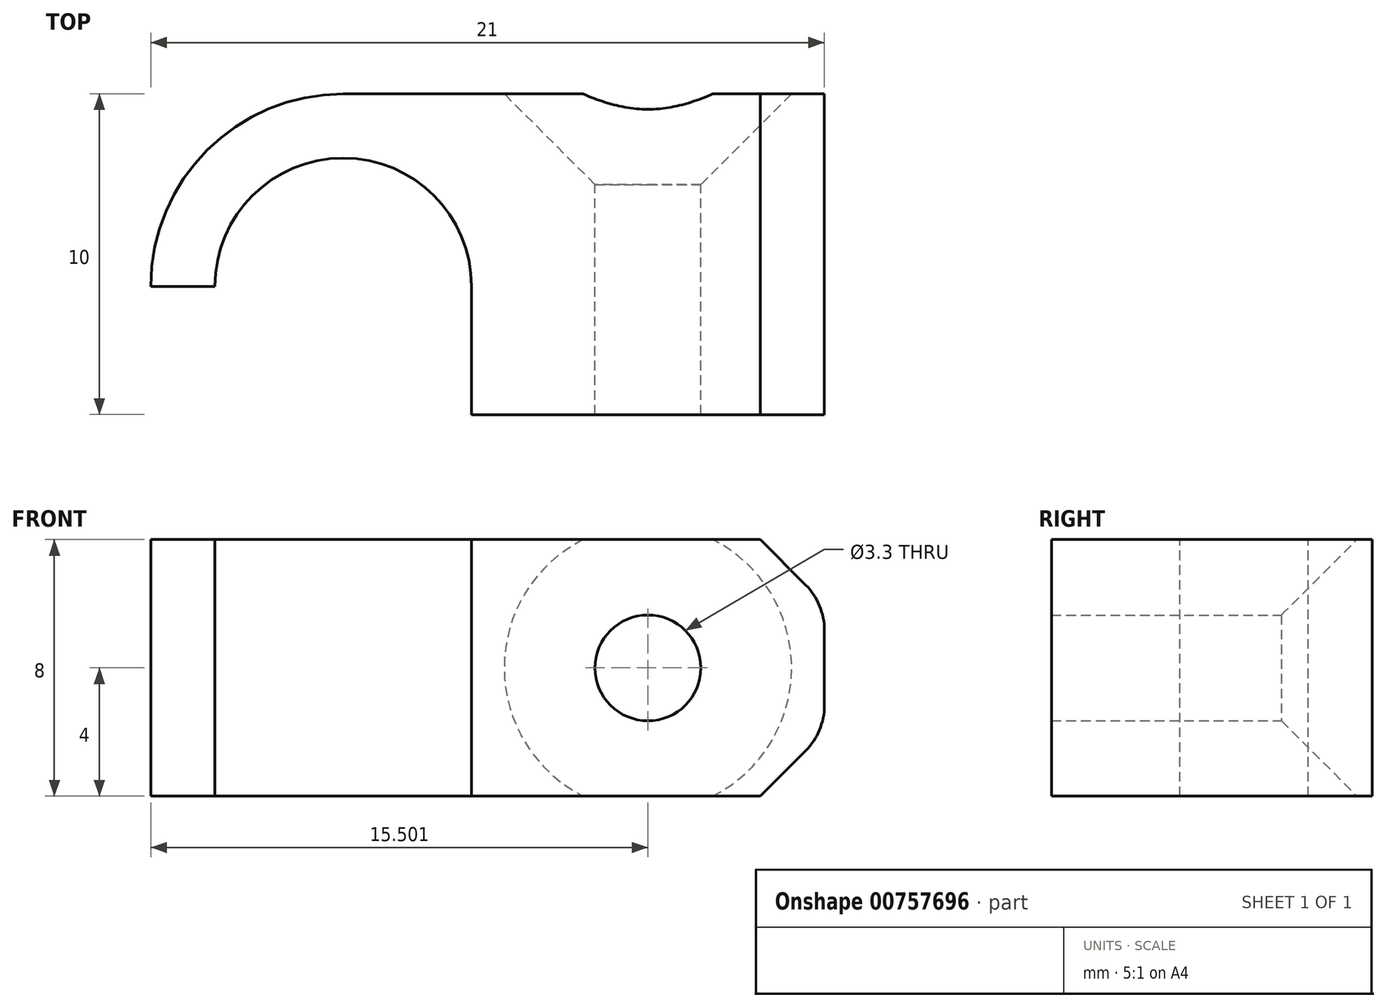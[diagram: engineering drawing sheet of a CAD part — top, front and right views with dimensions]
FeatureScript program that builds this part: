
annotation { "Feature Type Name" : "Feature", "Feature Type Description" : "" }
export const myFeature = defineFeature(function(context is Context, id is Id, definition is map)
    precondition{}
    {
        {
            var Q0;
            Q0=qCreatedBy(makeId("Top.planeOp"),FACE);
            var sketch = newSketch(context, id + "F0", { "sketchPlane" : qUnion([Q0])});
            skArc(sketch, "E0", {"start": v(-7.6, 12.22) * mm, "mid": v(-11.6, 16.22) * mm, "end": v(-15.6, 12.22) * mm});
            skArc(sketch, "E1.0", {"start": v(-11.6, 18.22) * mm, "mid": v(-15.84, 16.46) * mm, "end": v(-17.6, 12.22) * mm});
            skLineSegment(sketch, "E2", {"start": v(-11.6, 18.22) * mm, "end": v(3.4, 18.22) * mm});
            skLineSegment(sketch, "E3", {"start": v(3.4, 18.22) * mm, "end": v(3.4, 8.22) * mm});
            skLineSegment(sketch, "E4", {"start": v(3.4, 8.22) * mm, "end": v(-7.6, 8.22) * mm});
            skLineSegment(sketch, "E5", {"start": v(-17.6, 12.22) * mm, "end": v(-15.6, 12.22) * mm});
            skLineSegment(sketch, "E6", {"start": v(-7.6, 12.22) * mm, "end": v(-7.6, 8.22) * mm});
            skPoint(sketch, "E7.orphan", {"position": v(-11.6, 8.22) * mm});
            skSolve(sketch);
        }
        {
            var Q0;
            Q0 = qSketchRegion(id + "F0", true);
            extrude(context, id + "F1", {"entities" : qUnion([Q0]), "endBound" : BoundingType.SYMMETRIC, "oppositeDirection" : true, "depth" : 8 * mm, "offsetDistance" : 25 * mm});
        }
        {
            var Q0;
            Q0=makeQuery(id+"F1.opExtrude","SWEPT_FACE",FACE,{"disambiguationData":[OSD([sQuery(id+"F0.wireOp",EDGE,"E2")])]});
            var sketch = newSketch(context, id + "F2", { "sketchPlane" : qUnion([Q0])});
            skLineSegment(sketch, "E8", {"start": v(-3.4, 4) * mm, "end": v(7.6, -4) * mm, "construction": true});
            skPoint(sketch, "E9", {"position": v(2.1, 0) * mm});
            skSolve(sketch);
        }
        {
            var Q0;
            Q0=sQuery(id+"F2.wireOp",VERTEX,"E9");
            var Q1;
            Q1=makeQuery(id+"F1.opExtrude","SWEPT_BODY",BODY,{"disambiguationData":[OSD([sQuery(id+"F0.wireOp",EDGE,"E0"),sQuery(id+"F0.wireOp",EDGE,"E1.0"),sQuery(id+"F0.wireOp",EDGE,"E2"),sQuery(id+"F0.wireOp",EDGE,"E3"),sQuery(id+"F0.wireOp",EDGE,"E4"),sQuery(id+"F0.wireOp",EDGE,"E5"),sQuery(id+"F0.wireOp",EDGE,"E6")])]});
            hole(context, id + "F3", {"style" : HoleStyle.C_SINK, "endStyle" : HoleEndStyle.THROUGH, "standardTappedOrClearance" : lookupTablePath({ "standard" : "ISO", "engagement" : "75%", "pitch" : "0.7 mm", "size" : "M4", "type" : "Tapped" }), "standardBlindInLast" : lookupTablePath({ "standard" : "ISO", "engagement" : "75%", "pitch" : "0.7 mm", "size" : "M4", "type" : "Tapped" }), "holeDiameter" : 3.3 * mm, "cSinkDiameter" : 8.96 * mm, "cSinkAngle" : 90 * degree, "majorDiameter" : 4 * mm, "showTappedDepth" : true, "isTappedThrough" : true, "tappedDepth" : 12 * mm, "tapClearance" : 3, "locations" : qUnion([Q0]), "scope" : qUnion([Q1])});
        }
        {
            var Q0;
            Q0=makeQuery(id+"F1.opExtrude","CAP_EDGE",EDGE,{"disambiguationData":[OSD([sQuery(id+"F0.wireOp",EDGE,"E3")])],"isStart":true});
            var Q1;
            Q1=makeQuery(id+"F1.opExtrude","CAP_EDGE",EDGE,{"disambiguationData":[OSD([sQuery(id+"F0.wireOp",EDGE,"E3")])],"isStart":false});
            chamfer(context, id + "F4", {"entities" : qUnion([Q0, Q1]), "width" : 2 * mm, "tangentPropagation" : true});
        }
        {
            var Q0;
            {var subQ0=sQuery(id+"F0.wireOp",EDGE,"E3");Q0=makeQuery(id+"F4.opChamfer","BLEND_EDGE",EDGE,{"blendedFrom":[makeQuery(id+"F1.opExtrude","CAP_EDGE",EDGE,{"disambiguationData":[OSD([subQ0])],"isStart":true}),makeQuery(id+"F1.opExtrude","SWEPT_FACE",FACE,{"disambiguationData":[OSD([subQ0])]})],"blendedInto":[makeQuery(id+"F1.opExtrude","SWEPT_FACE",FACE,{"disambiguationData":[OSD([subQ0])]})]});}
            var Q1;
            {var subQ0=sQuery(id+"F0.wireOp",EDGE,"E3");Q1=makeQuery(id+"F4.opChamfer","BLEND_EDGE",EDGE,{"blendedFrom":[makeQuery(id+"F1.opExtrude","CAP_EDGE",EDGE,{"disambiguationData":[OSD([subQ0])],"isStart":false}),makeQuery(id+"F1.opExtrude","SWEPT_FACE",FACE,{"disambiguationData":[OSD([subQ0])]})],"blendedInto":[makeQuery(id+"F1.opExtrude","SWEPT_FACE",FACE,{"disambiguationData":[OSD([subQ0])]})]});}
            fillet(context, id + "F5", {"entities" : qUnion([Q0, Q1]), "radius" : 2 * mm, "tangentPropagation" : true, "allowEdgeOverflow" : false});
        }
    });
